# Revit family: SLICK.PRS AGRO LED
name_source: partatom
category: Осветительные приборы
revit_build: Autodesk Revit 2016 (Build: 20150220_1215(x64)
units: mm (PartAtom-declared; Revit-internal decimal feet)

## family parameters
Источник света = Да
Общий = Нет
Основа = Грань
При загрузке вырезать с полостями = Нет
Размер круглого соединителя = Использовать диаметр
Тип детали = Нормальный
Точка расчета площади = Нет

## types (1)
- SLICK.PRS AGRO LED
    ADSK_Единица измерения = Шт.
    ADSK_Завод-изготовитель = ООО МГК Световые технологии
    ADSK_Код изделия = 1631001330
    ADSK_Количество фаз = 1
    ADSK_Количество фаз числовое = 1
    ADSK_Коэффициент мощности = 0.96
    ADSK_Масса = 2.2
    ADSK_Наименование = Надежный светильник с высокой степенью IP для освещения сельскохозяйственных помещений. Корпус из литого под давлением алюминия и рассеиватель из ABS-пластика устойчивы к воздействию аммиака. Широкий список опций включает в себя модификации с управлением по протоколу DALI, сквозную проводку, различные варианты цветовой температуры
    ADSK_Напряжение = 230 В
    ADSK_Номинальная мощность = 0 кВт
    ADSK_Полная мощность = 0 кВ·А
    ADSK_Размер_Высота = 86 мм
    ADSK_Размер_Длина = 953 мм
    ADSK_Размер_Ширина = 96 мм
    ADSK_Ток = 0 А
    ADSK_Энергоэффективность = 117 лм/Вт
    IP Class = IP65
    URL = https://www.ltcompany.com
    Блок аварийного питания = Нет
    Видимая форма излучения при визуализации = Нет
    Группа модели = Светильники
    Изготовитель = ООО МГК Световые технологии
    Излучение по длине прямоугольника = 953 мм
    Излучение по ширине прямоугольника = 96 мм
    Класс Защиты = I
    Класс пожароопасности = П-II,IIа
    Климатическая зона = УХЛ2
    Код по классификатору = D5020200
    Корпус = Cерый металл
    Крепление = 19 мм
    Область использования = Нефтегазовая промышленность, Промышленные предприятия, Теплицы (растениеводство)
    Описание = Надежный светильник с высокой степенью IP для освещения сельскохозяйственных помещений. Корпус из литого под давлением алюминия и рассеиватель из ABS-пластика устойчивы к воздействию аммиака. Широкий список опций включает в себя модификации с управлением по протоколу DALI, сквозную проводку, различные варианты цветовой температуры
    Отметка по умолчанию = 0 мм
    Плафон = Плафон самосвечение
    Подвес ширина = 300 мм
    Подвес.материал = Cерый металл
    Полная установленная мощность = 0 кВ·А
    Разработчик = ООО ПРОРУБИМ
    Разработчик (телефон) = +7 (495) 649-85-43
    Светофильтр = 16777215
    Смещение цветовой температуры при затухании лампы = <Нет>
    Тип ИС = LED
    Тип ПРА = Драйвер
    Тип продукции = Светильник
    Угол наклона = -90.00°
    Файл фотометрической сетки = generic

## geometry (parser evidence)
native form markers: Blend x2
no freeform markers — native parametric forms only
